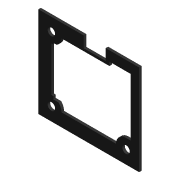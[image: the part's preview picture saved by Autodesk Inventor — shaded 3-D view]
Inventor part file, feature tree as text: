
AUTODESK INVENTOR PART (.ipt)
format: ipt  version: 2015 SP1 (Build 190203100, 203)  size: 179,712 bytes
history: native  units: mm
features: extrude x3, other x1, sketch x1
ambient origin geometry x8: Origin, YZ Plane, XZ Plane, XY Plane, X Axis, Y Axis, Z Axis, Center Point
bodies: Body1 (feature_tree)
feature tree (5):
  other  "Твердое тело1"
  extrude  "Выдавливание1"  Depth=1.0mm TaperAngle=0.0deg
  extrude  "Выдавливание2"  Depth=1.0mm TaperAngle=0.0deg
  extrude  "Выдавливание3"  Depth=1.0mm TaperAngle=0.0deg
  sketch  "Эскиз1"
